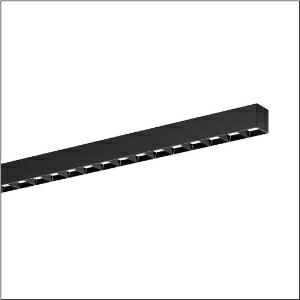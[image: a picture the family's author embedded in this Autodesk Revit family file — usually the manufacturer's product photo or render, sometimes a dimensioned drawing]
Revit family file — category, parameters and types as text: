
# Revit family: silica_r__21_51mx21dc3abb_8748
name_source: partatom
category: Lighting Fixtures
units: mm (PartAtom-declared; Revit-internal decimal feet)

## family parameters
Cut with Voids When Loaded = No
Host = Face
Light Source = No
Part Type = Normal
Room Calculation Point = No
Round Connector Dimension = Use Diameter
Shared = No

## types (1)
- --- (1 x LED, 10800 lm, 69.3 W, 3000K)
    Apparent Load = 69 VA
    CIE Flux Codes = 87 99 100 100 100
    Color Rendering = 80
    Color Temperature = 3000K
    Default Elevation = 1800 mm
    Description = Silica® 21, office luminaire, primary light control with darklight reflector, of PMMA, black, CAT 2 (L<= 3000cd/m²), light emission: direct distribution, primary light characteristic: symmetric, installation type: surface-mounted, LED, rated luminous flux: 10.800lm, luminous efficacy: 156lm/W, light colour: 830, colour temperature: 3000K, with terminal, 3+2-pole, max. 2.5mm², mains connection: 220..240V, AC, 50/60Hz, luminaire housing, of aluminium, jet black (RAL 9005), length: 3.004mm, width: 53mm, height: 53mm, protection rating (complete): IP20, insulation class (complete): insulation class I (protective earthing), certification: CE, permissible operating ambient temperature: 0..+35°C, standard: EN 50419, packaging unit: 1 piece
    Height = 0 mm  [stored 0 ft]
    Lamp = 1 x LED
    Lamp Light Flux = 10800 lm
    Lamp Power = 69.3 W
    Lamp count = 1
    Length = 3004 mm
    Luminous efficacy = 156 lm/W
    Manufacturer = Siteco
    ModVariant = No
    Model = 51MX21DC3ABB
    Mounting Place = Ceiling
    Mounting Type = Recessed
    Number of Poles = 1
    OnlyDefault = Yes
    Power Factor = 1
    Product Name = Silica® 21
    Product group = office luminaire | ceiling recessed
    ProductGroupID = 401
    Protection Class = Protection class I
    Protection Degree = IP 20
    RLX_Detail_Level = 1
    RLX_Emergency_Light_Flux = 0 lm
    RLX_Emergency_Type = 0
    RLX_Emergency_Type_DB = No
    RlxData = <blob elided: 64309 chars, md5=c9eb6a35>
    Socket = socket
    Standby Power = 0 W
    System Light Flux = 10800 lm
    System Power = 69 W
    Type Comments = factory setting: luminous flux: 100 % | dim-lin: 254 | 393 mA
    Type Image = l_1297756.jpg
    URL = http://relux.com
    VarID = @adj_054527
    Voltage = 0 V
    Weight = 0.00 kg
    Width = 53 mm

note: [stored X ft] marks values corroborated as IEEE doubles in the binary element streams (Revit-internal decimal feet)

## geometry (parser evidence)
native form markers: Blend x4, Sweep x9
no freeform markers — native parametric forms only
